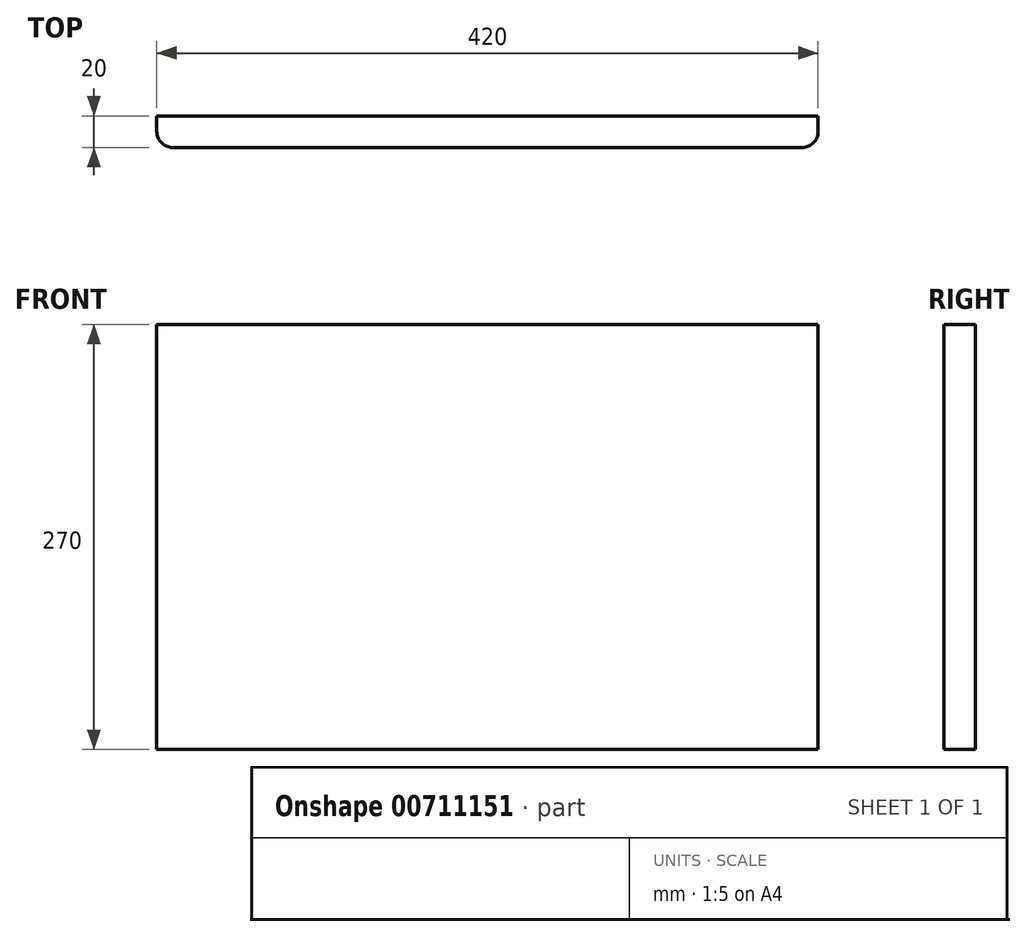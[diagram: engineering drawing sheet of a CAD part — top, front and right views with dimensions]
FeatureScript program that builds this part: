
annotation { "Feature Type Name" : "Feature", "Feature Type Description" : "" }
export const myFeature = defineFeature(function(context is Context, id is Id, definition is map)
    precondition{}
    {
        {
            var Q0;
            Q0=qCreatedBy(makeId("Front.planeOp"),FACE);
            var sketch = newSketch(context, id + "F0", { "sketchPlane" : qUnion([Q0])});
            skLineSegment(sketch, "E0.bottom", {"start": v(0, 0) * mm, "end": v(420, 0) * mm});
            skLineSegment(sketch, "E0.top", {"start": v(0, 270) * mm, "end": v(420, 270) * mm});
            skLineSegment(sketch, "E0.left", {"start": v(0, 0) * mm, "end": v(0, 270) * mm});
            skLineSegment(sketch, "E0.right", {"start": v(420, 0) * mm, "end": v(420, 270) * mm});
            skSolve(sketch);
        }
        {
            var Q0;
            Q0=makeQuery(id+"F0.imprint","IMPRINT",FACE,{"disambiguationData":[TD([[makeQuery(id+"F0.imprint","IMPRINT",EDGE,{"derivedFrom":sQuery(id+"F0.wireOp",EDGE,"E0.bottom")}),1.0]])]});
            extrude(context, id + "F1", {"entities" : qUnion([Q0]), "depth" : 20 * mm, "offsetDistance" : 25 * mm});
        }
        {
            var Q0;
            Q0=makeQuery(id+"F1.opExtrude","CAP_EDGE",EDGE,{"disambiguationData":[OSD([sQuery(id+"F0.wireOp",EDGE,"E0.right")])],"isStart":false});
            fillet(context, id + "F2", {"entities" : qUnion([Q0]), "radius" : 10 * mm, "tangentPropagation" : true, "allowEdgeOverflow" : false});
        }
        {
            var Q0;
            Q0=makeQuery(id+"F1.opExtrude","CAP_EDGE",EDGE,{"disambiguationData":[OSD([sQuery(id+"F0.wireOp",EDGE,"E0.left")])],"isStart":false});
            fillet(context, id + "F3", {"entities" : qUnion([Q0]), "radius" : 10 * mm, "tangentPropagation" : true, "allowEdgeOverflow" : false});
        }
    });
